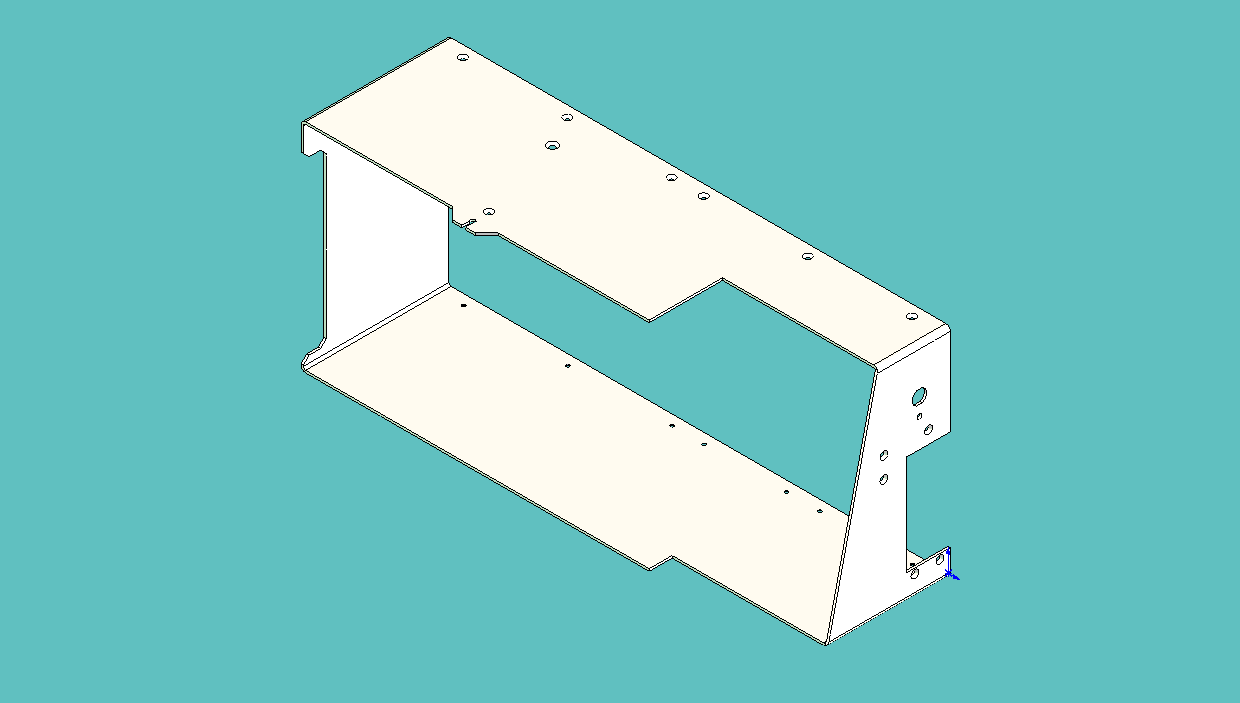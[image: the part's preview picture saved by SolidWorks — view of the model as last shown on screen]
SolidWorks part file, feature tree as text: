
SOLIDWORKS PART (.sldprt)
format: sldprt  version: not decoded by parser v0  size: 851,456 bytes
history: native  units: mm
features: sketch x9, cut_extrude x6, plane x3, chamfer x3, fillet x3, material x1, extrude x1, hole x1 (+10 scaffold rows collapsed)
feature tree (37):
  scaffold x10  (default folders/planes/origin — collapsed)
  material  "Matériau <non spécifié>"
  plane  "Plan de face"
  plane  "Plan de dessus"
  plane  "Plan de droite"
  sketch  "Esquisse1"  dims[D1=2.0mm D2=2.0mm D3=2.0mm D4=2.0mm D5=190.0mm D6=440.0mm]
  extrude  "Extrusion1"  Depth=137mm
  sketch  "Esquisse3"  dims[c1.D5=~8.556123mm c1.D7=4.0mm c1.D1=20.0mm c1.D2=40.0mm c1.D3=127.0mm c2.D2=127.0mm c2.D3=10.0mm c2.D4=3.0mm c2.D5=8.0mm c2.D6=152.0mm c2.D8=304.0mm c2.D9=63.0mm]
  cut_extrude  "Enlèv. mat.-Extru.1"  Depth=2mm
  sketch  "Esquisse4"  dims[c1.D1=10.0mm c1.D2=160.0mm c1.D3=107.0mm c1.D4=8.0mm c2.D1=160.0mm c2.D2=10.0mm]
  cut_extrude  "Enlèv. mat.-Extru.2"  Depth=2mm
  sketch  "Esquisse5"  dims[D1=107.0mm]
  cut_extrude  "Enlèv. mat.-Extru.3"  Depth=2mm
  sketch  "Esquisse6"  dims[c1.D6=12.6mm c1.D7=4.3mm c1.D11=3.0mm c1.D13=3.0mm c1.D15=3.0mm c1.D16=3.0mm c1.D1=22.5mm c1.D2=110.0mm c1.D3=38.0mm c1.D4=135.0mm c1.D5=40.0mm c1.D8=27.0mm c1.D9=11.5mm c1.D10=5.75mm c1.D12=22.0mm c2.D13=9.0mm c2.D14=18.0mm c2.D15=19.0mm c2.D16=58.0mm c2.D17=18.0mm c2.D18=11.0mm]
  cut_extrude  "Enlèv. mat.-Extru.4"  Depth=2mm
  chamfer  "Chanfrein1"  Distance=5mm Angle=45deg
  hole  "Fraisage pour vis à tête fraisée M2.51"  Diameter=3mm Depth=20mm
  sketch  "Esquisse3D1"  dims[D1=24.0mm D2=24.0mm D3=91.0mm D4=91.0mm D5=91.0mm D6=91.0mm D7=9.5mm D8=9.0mm D9=24.0mm D10=24.0mm D11=81.0mm D12=29.0mm D13=72.0mm D14=91.0mm D15=91.0mm D16=152.0mm D17=115.0mm]
  sketch  "Esquisse7"  dims[hole-wizard template sketch: 39 standard entries collapsed; hole parameters kept: c13.Diamètre du perçage=3.0mm c13.Profondeur du perçage=20.0mm c13.Diamètre du fraisage entrant=7.0mm c13.D4=~33.297463mm c13.Angle du fraisage entrant=90.0deg c14.D5=~14.816244mm c14.Angle de pointe=118.0deg]
  fillet  "Congé1"  Radius=2mm
  fillet  "Congé2"  Radius=4mm
  sketch  "Esquisse8"  dims[c1.D1=~34.385599mm c1.D3=5.0mm c2.D1=37.0mm c2.D2=129.5mm]
  cut_extrude  "Enlèv. mat.-Extru.5"  Depth=10mm
  chamfer  "Chanfrein2"  Distance=2mm Angle=45deg
  sketch  "Esquisse9"  dims[c1.D5=3.1mm c1.D10=3.0mm c1.D1=25.0mm c1.D2=~14.231691mm c2.D2=80.0deg c2.D3=5.7mm c2.D4=11.4mm c2.D6=20.5mm c2.D7=15.0mm c2.D8=47.0mm c2.D9=50.0mm c2.D11=33.0mm c2.D12=20.0mm c2.D13=36.0mm]
  cut_extrude  "Enlèv. mat.-Extru.6"  Depth=10mm
  fillet  "Congé3"  Radius=1.5mm
  chamfer  "Chanfrein3"  Distance=2mm Angle=45deg
decode coverage: 23 of 23 modeling features carry decoded parameters
note: ~ marks probable driven/reference dimensions
note: suppression state not decoded; provenance and decode notes live in map.json
